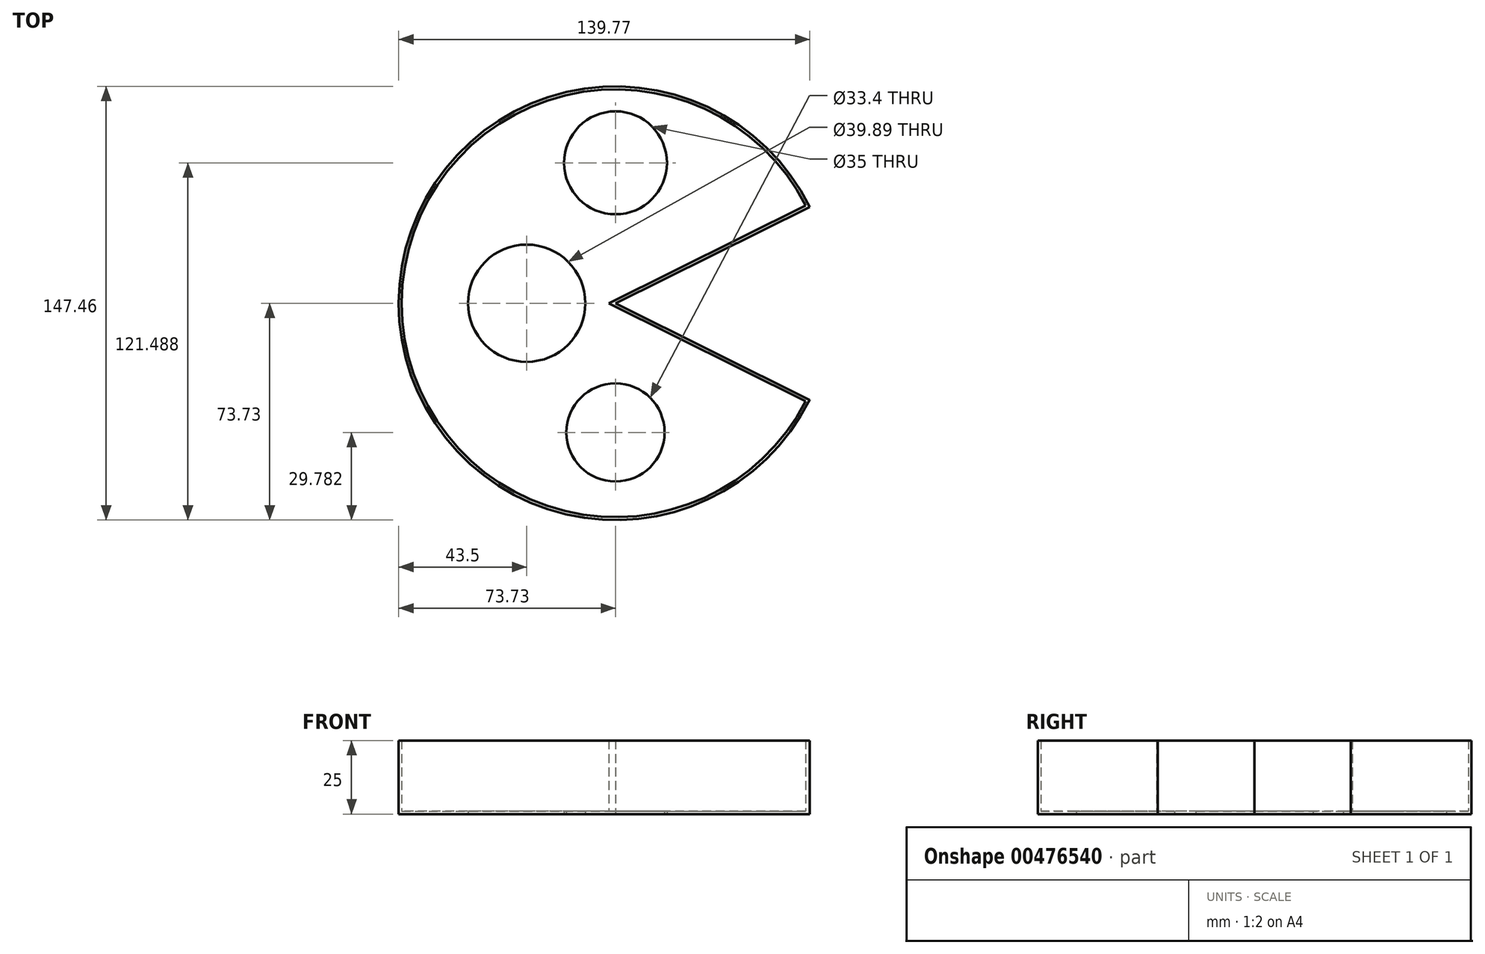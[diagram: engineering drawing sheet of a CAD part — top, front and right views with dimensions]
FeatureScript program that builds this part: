
annotation { "Feature Type Name" : "Feature", "Feature Type Description" : "" }
export const myFeature = defineFeature(function(context is Context, id is Id, definition is map)
    precondition{}
    {
        {
            var Q0;
            Q0=qCreatedBy(makeId("Top.planeOp"),FACE);
            var sketch = newSketch(context, id + "F0", { "sketchPlane" : qUnion([Q0])});
            skArc(sketch, "E0", {"start": v(66.04, 32.77) * mm, "mid": v(-73.73, 0.06) * mm, "end": v(66, -32.87) * mm});
            skLineSegment(sketch, "E1", {"start": v(0, 0) * mm, "end": v(66.04, 32.77) * mm});
            skLineSegment(sketch, "E2", {"start": v(0, 0) * mm, "end": v(66, -32.87) * mm});
            skSolve(sketch);
        }
        {
            var Q0;
            Q0 = qSketchRegion(id + "F0", true);
            extrude(context, id + "F1", {"entities" : qUnion([Q0]), "depth" : 25 * mm});
        }
        {
            var Q0;
            Q0=makeQuery(id+"F1.opExtrude","CAP_FACE",FACE,{"disambiguationData":[OSD([sQuery(id+"F0.wireOp",EDGE,"E0"),sQuery(id+"F0.wireOp",EDGE,"E1"),sQuery(id+"F0.wireOp",EDGE,"E2")])],"isStart":false});
            shell(context, id + "F2", {"entities" : qUnion([Q0]), "thickness" : 1 * mm});
        }
        {
            var Q0;
            Q0=qCreatedBy(makeId("Top.planeOp"),FACE);
            var sketch = newSketch(context, id + "F3", { "sketchPlane" : qUnion([Q0])});
            skCircle(sketch, "E3", {"center": v(0, -43.95) * mm, "radius": 16.7 * mm});
            skCircle(sketch, "E4", {"center": v(-30.23, 0) * mm, "radius": 19.95 * mm});
            skCircle(sketch, "E5", {"center": v(0, 47.76) * mm, "radius": 17.5 * mm});
            skSolve(sketch);
        }
        {
            var Q0;
            Q0=makeQuery(id+"F3.imprint","IMPRINT",FACE,{"disambiguationData":[TD([[makeQuery(id+"F3.imprint","IMPRINT",EDGE,{"derivedFrom":sQuery(id+"F3.wireOp",EDGE,"E5")}),1.0]])]});
            var Q1;
            Q1=makeQuery(id+"F3.imprint","IMPRINT",FACE,{"disambiguationData":[TD([[makeQuery(id+"F3.imprint","IMPRINT",EDGE,{"derivedFrom":sQuery(id+"F3.wireOp",EDGE,"E4")}),1.0]])]});
            var Q2;
            Q2=makeQuery(id+"F3.imprint","IMPRINT",FACE,{"disambiguationData":[TD([[makeQuery(id+"F3.imprint","IMPRINT",EDGE,{"derivedFrom":sQuery(id+"F3.wireOp",EDGE,"E3")}),1.0]])]});
            extrude(context, id + "F4", {"entities" : qUnion([Q0, Q1, Q2]), "operationType" : NewBodyOperationType.REMOVE, "depth" : 25 * mm});
        }
    });
